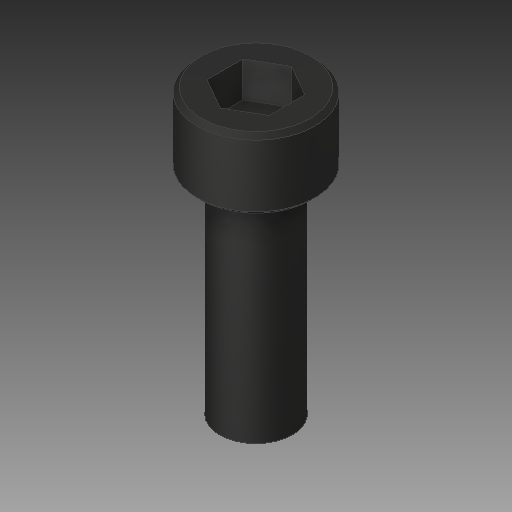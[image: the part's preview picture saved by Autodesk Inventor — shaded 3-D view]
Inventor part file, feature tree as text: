
AUTODESK INVENTOR PART (.ipt)
format: ipt  version: 2017 (Build 210142000, 142)  size: 105,472 bytes
history: native  units: in
note: dims shown in document units (in); Inventor stores cm internally (conversion verified against a paired STEP export)
features: chamfer x1
ambient origin geometry x8: Origin, YZ Plane, XZ Plane, XY Plane, X Axis, Y Axis, Z Axis, Center Point
bodies: Solid1 (feature_tree)
feature tree (1):
  chamfer  "Chamfer2"  [1 undecoded]
note: 1 required parameter value undecoded (feature->parameter linkage not recoverable at this tier; creation-order binding heuristic only, values carry confidence <= 0.55)
